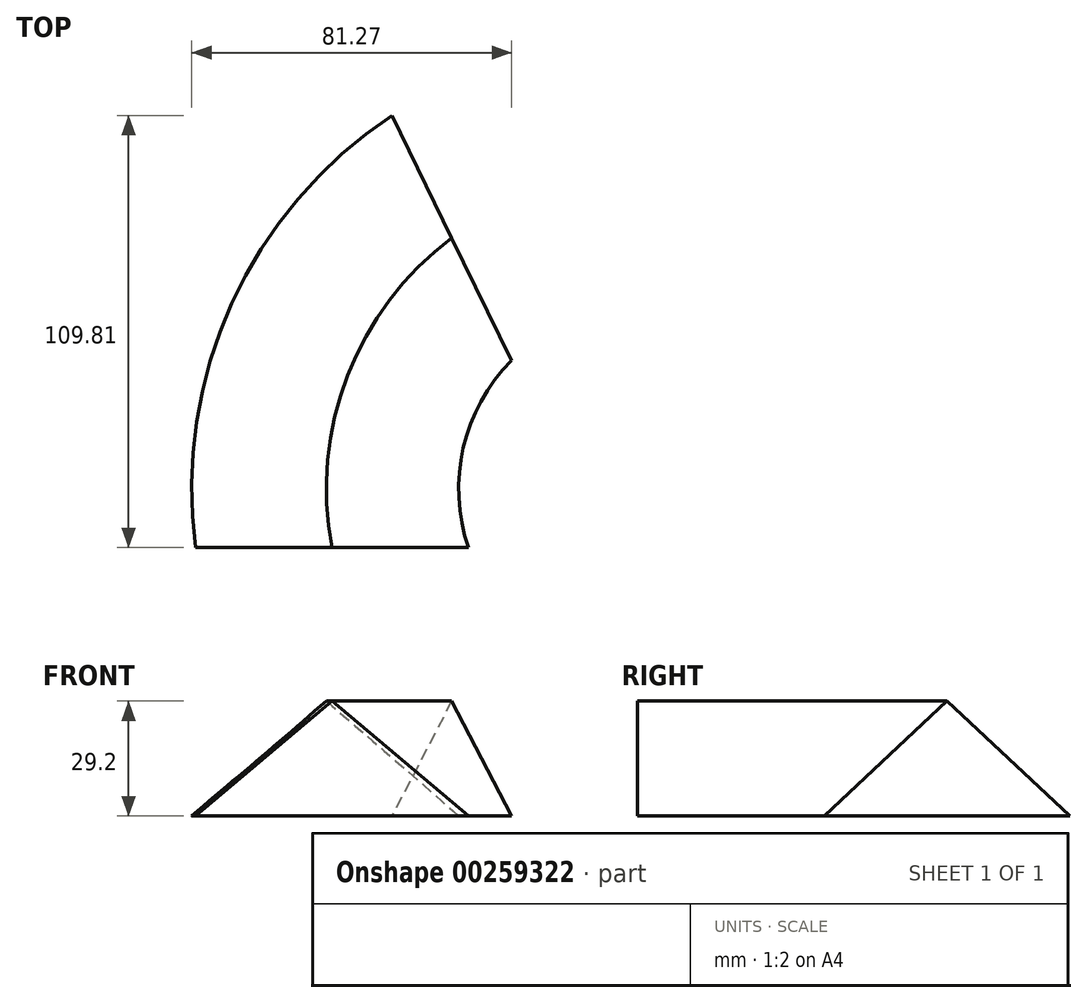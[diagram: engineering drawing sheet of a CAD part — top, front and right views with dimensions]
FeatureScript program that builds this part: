
annotation { "Feature Type Name" : "Feature", "Feature Type Description" : "" }
export const myFeature = defineFeature(function(context is Context, id is Id, definition is map)
    precondition{}
    {
        {
            var Q0;
            Q0=qCreatedBy(makeId("Front.planeOp"),FACE);
            var sketch = newSketch(context, id + "F0", { "sketchPlane" : qUnion([Q0])});
            skLineSegment(sketch, "E0", {"start": v(0, 29.2) * mm, "end": v(-34.66, 0) * mm});
            skLineSegment(sketch, "E1.MirrorCS", {"start": v(0, 29.2) * mm, "end": v(34.66, 0) * mm});
            skLineSegment(sketch, "E2", {"start": v(-34.66, 0) * mm, "end": v(34.66, 0) * mm});
            skSolve(sketch);
        }
        {
            var Q0;
            Q0=qCreatedBy(makeId("Top.planeOp"),FACE);
            var sketch = newSketch(context, id + "F1", { "sketchPlane" : qUnion([Q0])});
            skArc(sketch, "E3", {"start": v(35.78, 67.64) * mm, "mid": v(14.32, 37.2) * mm, "end": v(12.25, 0) * mm});
            skArc(sketch, "E4", {"start": v(12.25, 0) * mm, "mid": v(0.24, 36.4) * mm, "end": v(-22.87, 66.99) * mm});
            skSolve(sketch);
        }
        {
            var Q0;
            Q0=makeQuery(id+"F0.imprint","IMPRINT",FACE,{"disambiguationData":[TD([[makeQuery(id+"F0.imprint","IMPRINT",EDGE,{"derivedFrom":sQuery(id+"F0.wireOp",EDGE,"E0")}),1.0]])]});
            var Q1;
            Q1=sQuery(id+"F1.wireOp",EDGE,"E3");
            sweep(context, id + "F2", {"profiles" : qUnion([Q0]), "path" : qUnion([Q1])});
        }
    });
